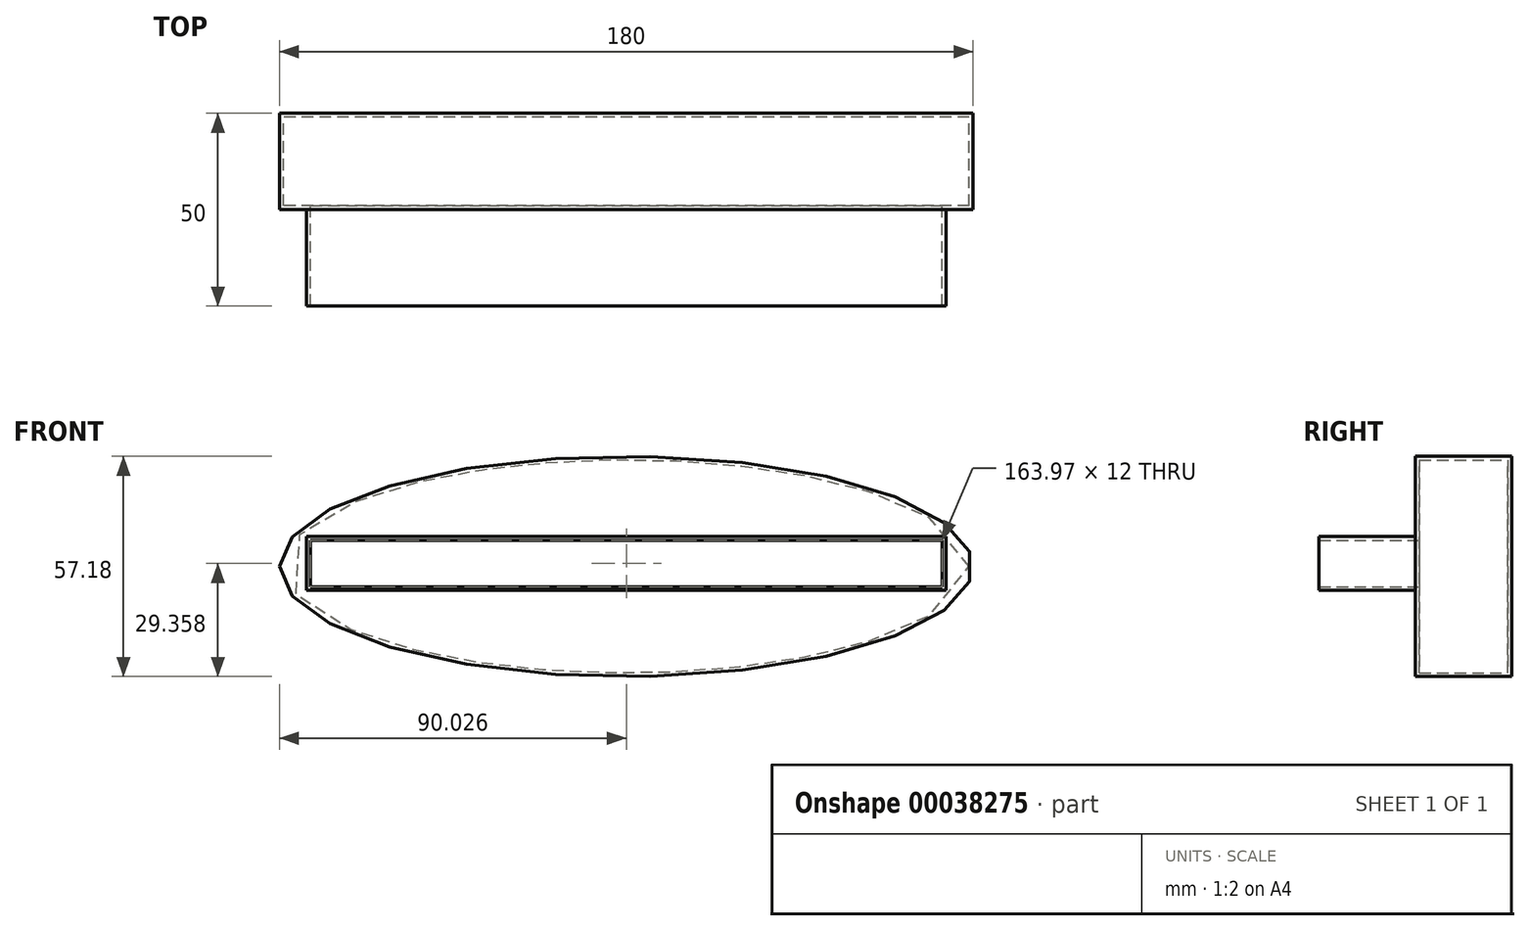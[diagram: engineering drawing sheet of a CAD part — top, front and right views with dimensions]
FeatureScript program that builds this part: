
annotation { "Feature Type Name" : "Feature", "Feature Type Description" : "" }
export const myFeature = defineFeature(function(context is Context, id is Id, definition is map)
    precondition{}
    {
        {
            var Q0;
            Q0=qCreatedBy(makeId("Front.planeOp"),FACE);
            var sketch = newSketch(context, id + "F0", { "sketchPlane" : qUnion([Q0])});
            skEllipse(sketch, "E0", {"center": v(0, 0) * mm, "majorRadius": 90 * mm, "minorRadius": 28.6 * mm, "majorAxis": v(-1, 0)});
            skLineSegment(sketch, "E1", {"start": v(-90, 0) * mm, "end": v(90, 0) * mm});
            skSolve(sketch);
        }
        {
            var Q0;
            {var subQ0=sQuery(id+"F0.wireOp",EDGE,"E1");Q0=makeQuery(id+"F0.imprint","IMPRINT",FACE,{"disambiguationData":[TD([[makeQuery(id+"F0.imprint","IMPRINT",EDGE,{"derivedFrom":subQ0}),-1.0]])]});}
            var Q1;
            {var subQ0=sQuery(id+"F0.wireOp",EDGE,"E1");Q1=makeQuery(id+"F0.imprint","IMPRINT",FACE,{"disambiguationData":[TD([[makeQuery(id+"F0.imprint","IMPRINT",EDGE,{"derivedFrom":subQ0}),1.0]])]});}
            extrude(context, id + "F1", {"entities" : qUnion([Q0, Q1]), "depth" : 25 * mm});
        }
        {
            var Q0;
            Q0=makeQuery(id+"F1.opExtrude","CAP_FACE",FACE,{"disambiguationData":[OSD([sQuery(id+"F0.wireOp",EDGE,"E0")])],"isStart":false});
            var sketch = newSketch(context, id + "F2", { "sketchPlane" : qUnion([Q0])});
            skLineSegment(sketch, "E2.bottom", {"start": v(-82.96, 7.77) * mm, "end": v(83.01, 7.77) * mm});
            skLineSegment(sketch, "E2.top", {"start": v(-82.96, -6.23) * mm, "end": v(83.01, -6.23) * mm});
            skLineSegment(sketch, "E2.left", {"start": v(-82.96, 7.77) * mm, "end": v(-82.96, -6.23) * mm});
            skLineSegment(sketch, "E2.right", {"start": v(83.01, 7.77) * mm, "end": v(83.01, -6.23) * mm});
            skSolve(sketch);
        }
        {
            var Q0;
            Q0=makeQuery(id+"F2.imprint","IMPRINT",FACE,{"disambiguationData":[TD([[makeQuery(id+"F2.imprint","IMPRINT",EDGE,{"derivedFrom":sQuery(id+"F2.wireOp",EDGE,"E2.bottom")}),-1.0]])]});
            extrude(context, id + "F3", {"entities" : qUnion([Q0]), "operationType" : NewBodyOperationType.ADD, "depth" : 25 * mm});
        }
        {
            var Q0;
            Q0=makeQuery(id+"F3.opExtrude","CAP_FACE",FACE,{"disambiguationData":[OSD([sQuery(id+"F2.wireOp",EDGE,"E2.bottom"),sQuery(id+"F2.wireOp",EDGE,"E2.top"),sQuery(id+"F2.wireOp",EDGE,"E2.left"),sQuery(id+"F2.wireOp",EDGE,"E2.right")])],"isStart":false});
            shell(context, id + "F4", {"entities" : qUnion([Q0]), "thickness" : 1 * mm});
        }
    });
